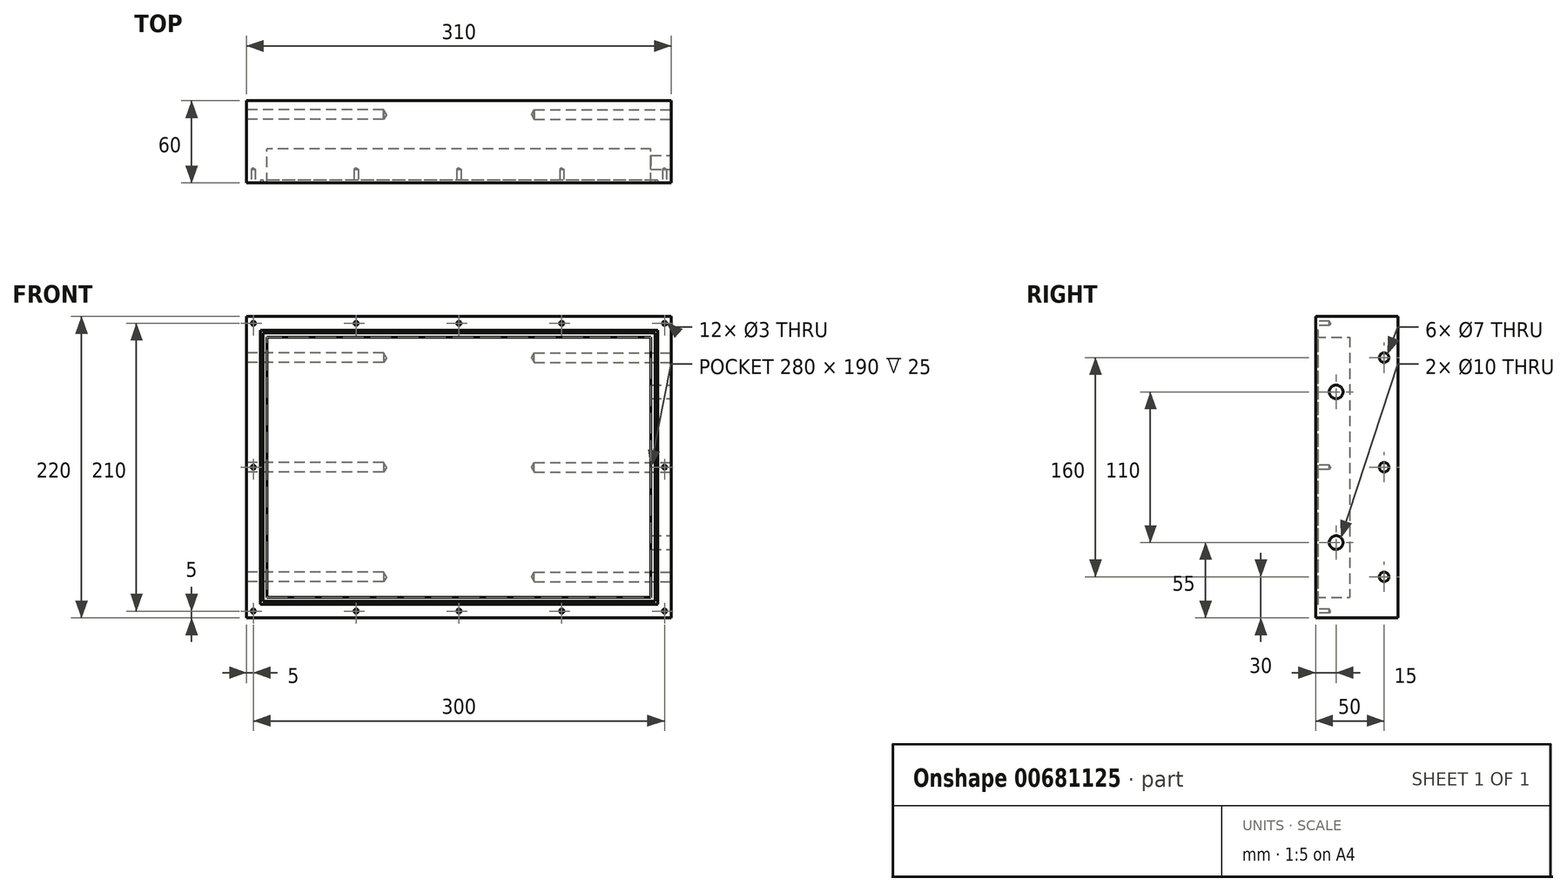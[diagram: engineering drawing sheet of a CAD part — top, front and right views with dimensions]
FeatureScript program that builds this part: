
annotation { "Feature Type Name" : "Feature", "Feature Type Description" : "" }
export const myFeature = defineFeature(function(context is Context, id is Id, definition is map)
    precondition{}
    {
        {
            var Q0;
            Q0=qCreatedBy(makeId("Front.planeOp"),FACE);
            var sketch = newSketch(context, id + "F0", { "sketchPlane" : qUnion([Q0])});
            skLineSegment(sketch, "E0.bottom", {"start": v(155, 110) * mm, "end": v(-155, 110) * mm});
            skLineSegment(sketch, "E0.top", {"start": v(155, -110) * mm, "end": v(-155, -110) * mm});
            skLineSegment(sketch, "E0.left", {"start": v(155, 110) * mm, "end": v(155, -110) * mm});
            skLineSegment(sketch, "E0.right", {"start": v(-155, 110) * mm, "end": v(-155, -110) * mm});
            skPoint(sketch, "E0.middle", {"position": v(0, 0) * mm});
            skPoint(sketch, "E1", {"position": v(-155, -110) * mm});
            skPoint(sketch, "E2", {"position": v(-155, 110) * mm});
            skSolve(sketch);
        }
        {
            var Q0;
            Q0=makeQuery(id+"F0.imprint","IMPRINT",FACE,{"disambiguationData":[TD([[makeQuery(id+"F0.imprint","IMPRINT",EDGE,{"derivedFrom":sQuery(id+"F0.wireOp",EDGE,"E0.bottom")}),1.0]])]});
            extrude(context, id + "F1", {"entities" : qUnion([Q0]), "depth" : 40 * mm, "offsetDistance" : 25 * mm});
        }
        {
            var Q0;
            Q0=makeQuery(id+"F1.opExtrude","CAP_FACE",FACE,{"disambiguationData":[OSD([sQuery(id+"F0.wireOp",EDGE,"E0.bottom"),sQuery(id+"F0.wireOp",EDGE,"E0.top"),sQuery(id+"F0.wireOp",EDGE,"E0.left"),sQuery(id+"F0.wireOp",EDGE,"E0.right")])],"isStart":false});
            shell(context, id + "F2", {"entities" : qUnion([Q0]), "thickness" : 15 * mm});
        }
        {
            var Q0;
            Q0=makeQuery(id+"F1.opExtrude","SWEPT_FACE",FACE,{"disambiguationData":[OSD([sQuery(id+"F0.wireOp",EDGE,"E0.left")])]});
            var sketch = newSketch(context, id + "F3", { "sketchPlane" : qUnion([Q0])});
            skPoint(sketch, "E3", {"position": v(-25, -55) * mm});
            skPoint(sketch, "E4", {"position": v(-25, 55) * mm});
            skSolve(sketch);
        }
        {
            var Q0;
            Q0=sQuery(id+"F3.wireOp",VERTEX,"E3");
            var Q1;
            Q1=sQuery(id+"F3.wireOp",VERTEX,"E4");
            var Q2;
            Q2=makeQuery(id+"F1.opExtrude","SWEPT_BODY",BODY,{"disambiguationData":[OSD([sQuery(id+"F0.wireOp",EDGE,"E0.bottom"),sQuery(id+"F0.wireOp",EDGE,"E0.top"),sQuery(id+"F0.wireOp",EDGE,"E0.left"),sQuery(id+"F0.wireOp",EDGE,"E0.right")])]});
            hole(context, id + "F4", {"style" : HoleStyle.SIMPLE, "endStyle" : HoleEndStyle.BLIND, "holeDiameter" : 10 * mm, "majorDiameter" : 5 * mm, "holeDepth" : 15 * mm, "isTappedThrough" : true, "tappedDepth" : 12 * mm, "tapClearance" : 3, "startFromSketch" : true, "locations" : qUnion([Q0, Q1]), "scope" : qUnion([Q2])});
        }
        {
            var Q0;
            Q0=makeQuery(id+"F1.opExtrude","CAP_FACE",FACE,{"disambiguationData":[OSD([sQuery(id+"F0.wireOp",EDGE,"E0.bottom"),sQuery(id+"F0.wireOp",EDGE,"E0.top"),sQuery(id+"F0.wireOp",EDGE,"E0.left"),sQuery(id+"F0.wireOp",EDGE,"E0.right")])],"isStart":false});
            var sketch = newSketch(context, id + "F5", { "sketchPlane" : qUnion([Q0])});
            skPoint(sketch, "E5", {"position": v(-150, 0) * mm});
            skPoint(sketch, "E5.positionSnap0", {"position": v(-140, 0) * mm});
            skPoint(sketch, "E6", {"position": v(-150, -105) * mm});
            skPoint(sketch, "E7", {"position": v(0, -105) * mm});
            skPoint(sketch, "E8", {"position": v(-75, -105) * mm});
            skPoint(sketch, "E9", {"position": v(75, -105) * mm});
            skPoint(sketch, "E10", {"position": v(150, -105) * mm});
            skPoint(sketch, "E11", {"position": v(-150, 105) * mm});
            skPoint(sketch, "E12", {"position": v(0, 105) * mm});
            skPoint(sketch, "E13", {"position": v(-75, 105) * mm});
            skPoint(sketch, "E14", {"position": v(75, 105) * mm});
            skPoint(sketch, "E15", {"position": v(150, 105) * mm});
            skPoint(sketch, "E16", {"position": v(150, 0) * mm});
            skPoint(sketch, "E16.positionSnap0", {"position": v(155, 0) * mm});
            skSolve(sketch);
        }
        {
            var Q0;
            Q0=sQuery(id+"F5.wireOp",VERTEX,"E6");
            var Q1;
            Q1=sQuery(id+"F5.wireOp",VERTEX,"E5");
            var Q2;
            Q2=sQuery(id+"F5.wireOp",VERTEX,"E11");
            var Q3;
            Q3=sQuery(id+"F5.wireOp",VERTEX,"E13");
            var Q4;
            Q4=sQuery(id+"F5.wireOp",VERTEX,"E8");
            var Q5;
            Q5=sQuery(id+"F5.wireOp",VERTEX,"E7");
            var Q6;
            Q6=sQuery(id+"F5.wireOp",VERTEX,"E9");
            var Q7;
            Q7=sQuery(id+"F5.wireOp",VERTEX,"E10");
            var Q8;
            Q8=sQuery(id+"F5.wireOp",VERTEX,"E16");
            var Q9;
            Q9=sQuery(id+"F5.wireOp",VERTEX,"E15");
            var Q10;
            Q10=sQuery(id+"F5.wireOp",VERTEX,"E14");
            var Q11;
            Q11=sQuery(id+"F5.wireOp",VERTEX,"E12");
            var Q12;
            Q12=makeQuery(id+"F1.opExtrude","SWEPT_BODY",BODY,{"disambiguationData":[OSD([sQuery(id+"F0.wireOp",EDGE,"E0.bottom"),sQuery(id+"F0.wireOp",EDGE,"E0.top"),sQuery(id+"F0.wireOp",EDGE,"E0.left"),sQuery(id+"F0.wireOp",EDGE,"E0.right")])]});
            hole(context, id + "F6", {"style" : HoleStyle.SIMPLE, "endStyle" : HoleEndStyle.BLIND, "holeDiameter" : 3 * mm, "majorDiameter" : 5 * mm, "holeDepth" : 10 * mm, "isTappedThrough" : true, "tappedDepth" : 12 * mm, "tapClearance" : 3, "startFromSketch" : true, "locations" : qUnion([Q0, Q1, Q2, Q3, Q4, Q5, Q6, Q7, Q8, Q9, Q10, Q11]), "scope" : qUnion([Q12])});
        }
        {
            var Q0;
            Q0=makeQuery(id+"F1.opExtrude","CAP_FACE",FACE,{"disambiguationData":[OSD([sQuery(id+"F0.wireOp",EDGE,"E0.bottom"),sQuery(id+"F0.wireOp",EDGE,"E0.top"),sQuery(id+"F0.wireOp",EDGE,"E0.left"),sQuery(id+"F0.wireOp",EDGE,"E0.right")])],"isStart":true});
            extrude(context, id + "F7", {"entities" : qUnion([Q0]), "operationType" : NewBodyOperationType.ADD, "depth" : 20 * mm, "offsetDistance" : 25 * mm});
        }
        {
            var Q0;
            {var subQ0=sQuery(id+"F0.wireOp",EDGE,"E0.right");Q0=makeQuery(id+"F7.boolean.opBoolean","MERGE",FACE,{"derivedFrom":[makeQuery(id+"F1.opExtrude","SWEPT_FACE",FACE,{"disambiguationData":[OSD([subQ0])]}),makeQuery(id+"F7.opExtrude","SWEPT_FACE",FACE,{"disambiguationData":[OSD([subQ0])]})]});}
            var sketch = newSketch(context, id + "F8", { "sketchPlane" : qUnion([Q0])});
            skPoint(sketch, "E17", {"position": v(-10, 80) * mm});
            skPoint(sketch, "E18", {"position": v(-10, 0) * mm});
            skPoint(sketch, "E19", {"position": v(-10, -80) * mm});
            skSolve(sketch);
        }
        {
            var Q0;
            Q0=sQuery(id+"F8.wireOp",VERTEX,"E17");
            var Q1;
            Q1=sQuery(id+"F8.wireOp",VERTEX,"E18");
            var Q2;
            Q2=sQuery(id+"F8.wireOp",VERTEX,"E19");
            var Q3;
            Q3=makeQuery(id+"F1.opExtrude","SWEPT_BODY",BODY,{"disambiguationData":[OSD([sQuery(id+"F0.wireOp",EDGE,"E0.bottom"),sQuery(id+"F0.wireOp",EDGE,"E0.top"),sQuery(id+"F0.wireOp",EDGE,"E0.left"),sQuery(id+"F0.wireOp",EDGE,"E0.right")])]});
            hole(context, id + "F9", {"style" : HoleStyle.SIMPLE, "endStyle" : HoleEndStyle.BLIND, "holeDiameter" : 7 * mm, "majorDiameter" : 5 * mm, "holeDepth" : 100 * mm, "isTappedThrough" : true, "tappedDepth" : 12 * mm, "tapClearance" : 3, "startFromSketch" : true, "locations" : qUnion([Q0, Q1, Q2]), "scope" : qUnion([Q3])});
        }
        {
            var Q0;
            {var subQ0=sQuery(id+"F0.wireOp",EDGE,"E0.left");Q0=makeQuery(id+"F7.boolean.opBoolean","MERGE",FACE,{"derivedFrom":[makeQuery(id+"F1.opExtrude","SWEPT_FACE",FACE,{"disambiguationData":[OSD([subQ0])]}),makeQuery(id+"F7.opExtrude","SWEPT_FACE",FACE,{"disambiguationData":[OSD([subQ0])]})]});}
            var sketch = newSketch(context, id + "F10", { "sketchPlane" : qUnion([Q0])});
            skPoint(sketch, "E20", {"position": v(10, -80) * mm});
            skPoint(sketch, "E21", {"position": v(10, 0) * mm});
            skPoint(sketch, "E22", {"position": v(10, 80) * mm});
            skSolve(sketch);
        }
        {
            var Q0;
            Q0=sQuery(id+"F10.wireOp",VERTEX,"E20");
            var Q1;
            Q1=sQuery(id+"F10.wireOp",VERTEX,"E21");
            var Q2;
            Q2=sQuery(id+"F10.wireOp",VERTEX,"E22");
            var Q3;
            Q3=makeQuery(id+"F1.opExtrude","SWEPT_BODY",BODY,{"disambiguationData":[OSD([sQuery(id+"F0.wireOp",EDGE,"E0.bottom"),sQuery(id+"F0.wireOp",EDGE,"E0.top"),sQuery(id+"F0.wireOp",EDGE,"E0.left"),sQuery(id+"F0.wireOp",EDGE,"E0.right")])]});
            hole(context, id + "F11", {"style" : HoleStyle.SIMPLE, "endStyle" : HoleEndStyle.BLIND, "holeDiameter" : 7 * mm, "majorDiameter" : 5 * mm, "holeDepth" : 100 * mm, "isTappedThrough" : true, "tappedDepth" : 12 * mm, "tapClearance" : 3, "startFromSketch" : true, "locations" : qUnion([Q0, Q1, Q2]), "scope" : qUnion([Q3])});
        }
        {
            var Q0;
            Q0=makeQuery(id+"F1.opExtrude","CAP_FACE",FACE,{"disambiguationData":[OSD([sQuery(id+"F0.wireOp",EDGE,"E0.bottom"),sQuery(id+"F0.wireOp",EDGE,"E0.top"),sQuery(id+"F0.wireOp",EDGE,"E0.left"),sQuery(id+"F0.wireOp",EDGE,"E0.right")])],"isStart":false});
            var sketch = newSketch(context, id + "F12", { "sketchPlane" : qUnion([Q0])});
            skLineSegment(sketch, "E23.bottom", {"start": v(-143, -100) * mm, "end": v(-145, -100) * mm});
            skLineSegment(sketch, "E23.top", {"start": v(-143, 100) * mm, "end": v(-145, 100) * mm});
            skLineSegment(sketch, "E23.left", {"start": v(-143, -100) * mm, "end": v(-143, 100) * mm});
            skLineSegment(sketch, "E23.right", {"start": v(-145, -100) * mm, "end": v(-145, 100) * mm});
            skPoint(sketch, "E23.middle", {"position": v(-144, 0) * mm});
            skLineSegment(sketch, "E24.bottom", {"start": v(143, 98) * mm, "end": v(-143, 98) * mm});
            skLineSegment(sketch, "E24.top", {"start": v(143, 100) * mm, "end": v(-143, 100) * mm});
            skLineSegment(sketch, "E24.left", {"start": v(143, 98) * mm, "end": v(143, 100) * mm});
            skLineSegment(sketch, "E24.right", {"start": v(-143, 98) * mm, "end": v(-143, 100) * mm});
            skPoint(sketch, "E24.middle", {"position": v(0, 99) * mm});
            skLineSegment(sketch, "E25.MirrorCS", {"start": v(143, -100) * mm, "end": v(-143, -100) * mm});
            skLineSegment(sketch, "E26.MirrorCS", {"start": v(143, -98) * mm, "end": v(-143, -98) * mm});
            skLineSegment(sketch, "E27.MirrorCS", {"start": v(143, -98) * mm, "end": v(143, -100) * mm});
            skLineSegment(sketch, "E28.MirrorCS", {"start": v(-143, -98) * mm, "end": v(-143, -100) * mm});
            skLineSegment(sketch, "E29.MirrorCS", {"start": v(143, -100) * mm, "end": v(143, 100) * mm});
            skLineSegment(sketch, "E30.MirrorCS", {"start": v(145, -100) * mm, "end": v(145, 100) * mm});
            skLineSegment(sketch, "E31.MirrorCS", {"start": v(143, 100) * mm, "end": v(145, 100) * mm});
            skLineSegment(sketch, "E32.MirrorCS", {"start": v(143, -100) * mm, "end": v(145, -100) * mm});
            skSolve(sketch);
        }
        {
            var Q0;
            Q0=makeQuery(id+"F12.imprint","IMPRINT",FACE,{"disambiguationData":[TD([[makeQuery(id+"F12.imprint","IMPRINT",EDGE,{"derivedFrom":sQuery(id+"F12.wireOp",EDGE,"E23.bottom")}),-1.0]])]});
            var Q1;
            {var subQ0=sQuery(id+"F12.wireOp",EDGE,"E25.MirrorCS");Q1=makeQuery(id+"F12.imprint","IMPRINT",FACE,{"disambiguationData":[TD([[makeQuery(id+"F12.imprint","IMPRINT",EDGE,{"derivedFrom":subQ0}),-1.0]])]});}
            var Q2;
            Q2=makeQuery(id+"F12.imprint","IMPRINT",FACE,{"disambiguationData":[TD([[makeQuery(id+"F12.imprint","IMPRINT",EDGE,{"derivedFrom":sQuery(id+"F12.wireOp",EDGE,"E30.MirrorCS")}),1.0]])]});
            var Q3;
            {var subQ0=sQuery(id+"F12.wireOp",EDGE,"E24.bottom");Q3=makeQuery(id+"F12.imprint","IMPRINT",FACE,{"disambiguationData":[TD([[makeQuery(id+"F12.imprint","IMPRINT",EDGE,{"derivedFrom":subQ0}),-1.0]])]});}
            extrude(context, id + "F13", {"entities" : qUnion([Q0, Q1, Q2, Q3]), "operationType" : NewBodyOperationType.REMOVE, "oppositeDirection" : true, "depth" : 2 * mm, "offsetDistance" : 25 * mm});
        }
    });
